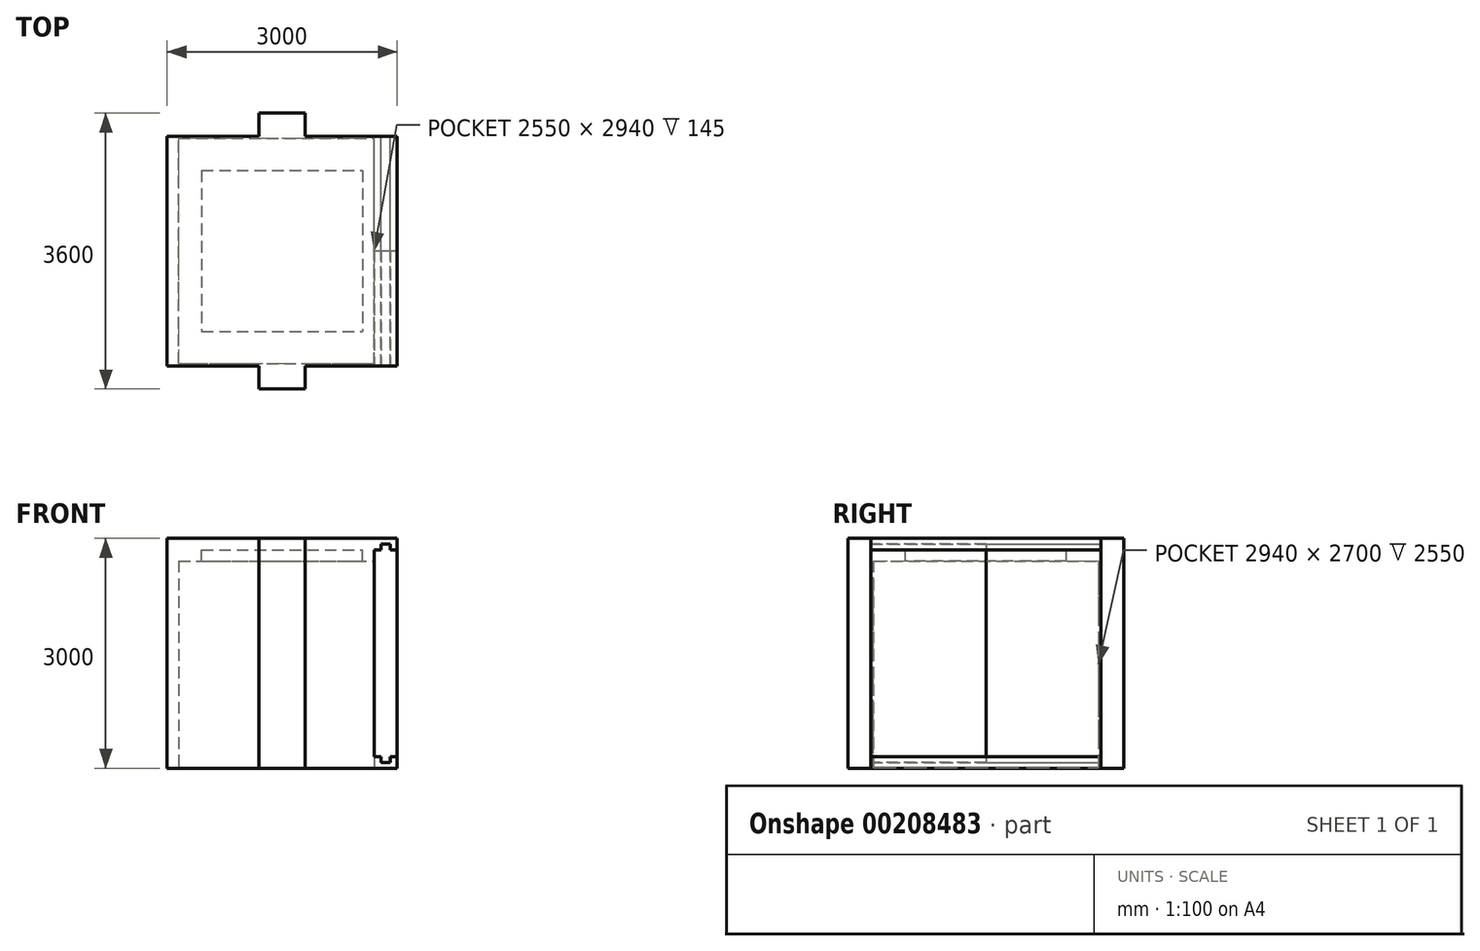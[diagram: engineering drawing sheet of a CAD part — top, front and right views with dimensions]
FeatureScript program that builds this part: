
annotation { "Feature Type Name" : "Feature", "Feature Type Description" : "" }
export const myFeature = defineFeature(function(context is Context, id is Id, definition is map)
    precondition{}
    {
        {
            var Q0;
            Q0=qCreatedBy(makeId("Top.planeOp"),FACE);
            var sketch = newSketch(context, id + "F0", { "sketchPlane" : qUnion([Q0])});
            skLineSegment(sketch, "E0.bottom", {"start": v(-1500, 1500) * mm, "end": v(1200, 1500) * mm});
            skLineSegment(sketch, "E0.top", {"start": v(-1500, -1500) * mm, "end": v(1200, -1500) * mm});
            skLineSegment(sketch, "E0.left", {"start": v(-1500, 1500) * mm, "end": v(-1500, -1500) * mm});
            skPoint(sketch, "E0.middle", {"position": v(0, 0) * mm});
            skLineSegment(sketch, "E1", {"start": v(-300, 1500) * mm, "end": v(-300, 1800) * mm});
            skLineSegment(sketch, "E2", {"start": v(-300, 1800) * mm, "end": v(300, 1800) * mm});
            skLineSegment(sketch, "E3", {"start": v(300, 1800) * mm, "end": v(300, 1500) * mm});
            skLineSegment(sketch, "E4.MirrorCS", {"start": v(-300, -1500) * mm, "end": v(-300, -1800) * mm});
            skLineSegment(sketch, "E5.MirrorCS", {"start": v(-300, -1800) * mm, "end": v(300, -1800) * mm});
            skLineSegment(sketch, "E6.MirrorCS", {"start": v(300, -1800) * mm, "end": v(300, -1500) * mm});
            skLineSegment(sketch, "E7", {"start": v(1200, 1500) * mm, "end": v(1200, -1500) * mm});
            skPoint(sketch, "E8.start.orphan", {"position": v(1200, 0) * mm});
            skSolve(sketch);
        }
        {
            var Q0;
            Q0=qSketchRegion(id+"F0",true);
            extrude(context, id + "F1", {"entities" : qUnion([Q0]), "depth" : 3000 * mm});
        }
        {
            var Q0;
            Q0=makeQuery(id+"F1.opExtrude","CAP_FACE",FACE,{"disambiguationData":[OSD([sQuery(id+"F0.wireOp",EDGE,"E0.bottom"),sQuery(id+"F0.wireOp",EDGE,"E0.top"),sQuery(id+"F0.wireOp",EDGE,"E0.left"),sQuery(id+"F0.wireOp",EDGE,"E0.right"),sQuery(id+"F0.wireOp",EDGE,"E1"),sQuery(id+"F0.wireOp",EDGE,"E2"),sQuery(id+"F0.wireOp",EDGE,"E3"),sQuery(id+"F0.wireOp",EDGE,"E4.MirrorCS"),sQuery(id+"F0.wireOp",EDGE,"E5.MirrorCS"),sQuery(id+"F0.wireOp",EDGE,"E6.MirrorCS")])],"isStart":false});
            var sketch = newSketch(context, id + "F2", { "sketchPlane" : qUnion([Q0])});
            skLineSegment(sketch, "E9.bottom", {"start": v(-1050, 1050) * mm, "end": v(1050, 1050) * mm});
            skLineSegment(sketch, "E9.top", {"start": v(-1050, -1050) * mm, "end": v(1050, -1050) * mm});
            skLineSegment(sketch, "E9.left", {"start": v(-1050, 1050) * mm, "end": v(-1050, -1050) * mm});
            skLineSegment(sketch, "E9.right", {"start": v(1050, 1050) * mm, "end": v(1050, -1050) * mm});
            skPoint(sketch, "E9.middle", {"position": v(0, 0) * mm});
            skSolve(sketch);
        }
        {
            var Q0;
            Q0=qSketchRegion(id+"F2",true);
            extrude(context, id + "F3", {"entities" : qUnion([Q0]), "operationType" : NewBodyOperationType.REMOVE, "oppositeDirection" : true, "depth" : 3000 * mm});
        }
        {
            var Q0;
            Q0=qCreatedBy(makeId("Top.planeOp"),FACE);
            var sketch = newSketch(context, id + "F4", { "sketchPlane" : qUnion([Q0])});
            skLineSegment(sketch, "E10.bottom", {"start": v(-1050, 1050) * mm, "end": v(1050, 1050) * mm});
            skLineSegment(sketch, "E10.top", {"start": v(-1050, -1050) * mm, "end": v(1050, -1050) * mm});
            skLineSegment(sketch, "E10.left", {"start": v(-1050, 1050) * mm, "end": v(-1050, -1050) * mm});
            skLineSegment(sketch, "E10.right", {"start": v(1050, 1050) * mm, "end": v(1050, -1050) * mm});
            skPoint(sketch, "E10.middle", {"position": v(0, 0) * mm});
            skSolve(sketch);
        }
        {
            var Q0;
            Q0=qSketchRegion(id+"F4",true);
            extrude(context, id + "F5", {"entities" : qUnion([Q0]), "operationType" : NewBodyOperationType.ADD, "depth" : 150 * mm});
        }
        {
            var Q0;
            Q0=makeQuery(id+"F1.opExtrude","CAP_FACE",FACE,{"disambiguationData":[OSD([sQuery(id+"F0.wireOp",EDGE,"E0.bottom"),sQuery(id+"F0.wireOp",EDGE,"E0.top"),sQuery(id+"F0.wireOp",EDGE,"E0.left"),sQuery(id+"F0.wireOp",EDGE,"E0.right"),sQuery(id+"F0.wireOp",EDGE,"E1"),sQuery(id+"F0.wireOp",EDGE,"E2"),sQuery(id+"F0.wireOp",EDGE,"E3"),sQuery(id+"F0.wireOp",EDGE,"E4.MirrorCS"),sQuery(id+"F0.wireOp",EDGE,"E5.MirrorCS"),sQuery(id+"F0.wireOp",EDGE,"E6.MirrorCS")])],"isStart":false});
            var sketch = newSketch(context, id + "F6", { "sketchPlane" : qUnion([Q0])});
            skLineSegment(sketch, "E11.bottom", {"start": v(-1050, 1050) * mm, "end": v(1050, 1050) * mm});
            skLineSegment(sketch, "E11.top", {"start": v(-1050, -1050) * mm, "end": v(1050, -1050) * mm});
            skLineSegment(sketch, "E11.left", {"start": v(-1050, 1050) * mm, "end": v(-1050, -1050) * mm});
            skLineSegment(sketch, "E11.right", {"start": v(1050, 1050) * mm, "end": v(1050, -1050) * mm});
            skPoint(sketch, "E11.middle", {"position": v(0, 0) * mm});
            skSolve(sketch);
        }
        {
            var Q0;
            Q0=qSketchRegion(id+"F6",true);
            extrude(context, id + "F7", {"entities" : qUnion([Q0]), "operationType" : NewBodyOperationType.ADD, "oppositeDirection" : true, "depth" : 150 * mm});
        }
        {
            var Q0;
            {var subQ0=sQuery(id+"F0.wireOp",EDGE,"E0.bottom");Q0=makeQuery(id+"F1.opExtrude","SWEPT_FACE",FACE,{"disambiguationData":[OSD([subQ0]),TDD([makeQuery(id+"F0.imprint","IMPRINT",EDGE,{"disambiguationData":[TD([[makeQuery(id+"F0.imprint","INTERSECT",VERTEX,{"derivedFrom":[subQ0,sQuery(id+"F0.wireOp",EDGE,"E7")]}),1.0]])],"derivedFrom":subQ0})])]});}
            var sketch = newSketch(context, id + "F8", { "sketchPlane" : qUnion([Q0])});
            skLineSegment(sketch, "E12", {"start": v(-1200, 3000) * mm, "end": v(-1500, 3000) * mm});
            skLineSegment(sketch, "E13", {"start": v(-1500, 3000) * mm, "end": v(-1500, 2850) * mm});
            skLineSegment(sketch, "E14", {"start": v(-1500, 2850) * mm, "end": v(-1410, 2850) * mm});
            skLineSegment(sketch, "E15", {"start": v(-1410, 2850) * mm, "end": v(-1410, 2925) * mm});
            skLineSegment(sketch, "E16", {"start": v(-1410, 2925) * mm, "end": v(-1290, 2925) * mm});
            skLineSegment(sketch, "E17", {"start": v(-1290, 2925) * mm, "end": v(-1290, 2850) * mm});
            skLineSegment(sketch, "E18", {"start": v(-1290, 2850) * mm, "end": v(-1200, 2850) * mm});
            skLineSegment(sketch, "E19", {"start": v(-1200, 3000) * mm, "end": v(-1200, 2850) * mm});
            skSolve(sketch);
        }
        {
            var Q0;
            Q0=qSketchRegion(id+"F8",true);
            extrude(context, id + "F9", {"entities" : qUnion([Q0]), "operationType" : NewBodyOperationType.ADD, "oppositeDirection" : true, "depth" : 3000 * mm});
        }
        {
            var Q0;
            Q0=makeQuery(id+"F1.opExtrude","SWEPT_FACE",FACE,{"disambiguationData":[OSD([sQuery(id+"F0.wireOp",EDGE,"E7")])]});
            var sketch = newSketch(context, id + "F10", { "sketchPlane" : qUnion([Q0])});
            skLineSegment(sketch, "E20.bottom", {"start": v(-1470, 2705) * mm, "end": v(1470, 2705) * mm});
            skLineSegment(sketch, "E20.top", {"start": v(-1470, 5) * mm, "end": v(1470, 5) * mm});
            skLineSegment(sketch, "E20.left", {"start": v(-1470, 2705) * mm, "end": v(-1470, 5) * mm});
            skLineSegment(sketch, "E20.right", {"start": v(1470, 2705) * mm, "end": v(1470, 5) * mm});
            skPoint(sketch, "E20.middle", {"position": v(0, 1355) * mm});
            skSolve(sketch);
        }
        {
            var Q0;
            Q0=qSketchRegion(id+"F10",true);
            extrude(context, id + "F11", {"entities" : qUnion([Q0]), "operationType" : NewBodyOperationType.REMOVE, "oppositeDirection" : true, "depth" : 2550 * mm});
        }
        {
            var Q0;
            {var subQ0=sQuery(id+"F0.wireOp",EDGE,"E0.bottom");Q0=makeQuery(id+"F9.boolean.opBoolean","MERGE",FACE,{"derivedFrom":[makeQuery(id+"F1.opExtrude","SWEPT_FACE",FACE,{"disambiguationData":[OSD([subQ0]),TDD([makeQuery(id+"F0.imprint","IMPRINT",EDGE,{"disambiguationData":[TD([[makeQuery(id+"F0.imprint","INTERSECT",VERTEX,{"derivedFrom":[subQ0,sQuery(id+"F0.wireOp",EDGE,"E7")]}),1.0]])],"derivedFrom":subQ0})])]}),makeQuery(id+"F9.opExtrude","CAP_FACE",FACE,{"disambiguationData":[OSD([sQuery(id+"F8.wireOp",EDGE,"E12"),sQuery(id+"F8.wireOp",EDGE,"E13"),sQuery(id+"F8.wireOp",EDGE,"E14"),sQuery(id+"F8.wireOp",EDGE,"E15"),sQuery(id+"F8.wireOp",EDGE,"E16"),sQuery(id+"F8.wireOp",EDGE,"E17"),sQuery(id+"F8.wireOp",EDGE,"E18"),sQuery(id+"F8.wireOp",EDGE,"E19")])],"isStart":true})]});}
            var sketch = newSketch(context, id + "F12", { "sketchPlane" : qUnion([Q0])});
            skLineSegment(sketch, "E21", {"start": v(-1200, 0) * mm, "end": v(-1500, 0) * mm});
            skLineSegment(sketch, "E22", {"start": v(-1500, 0) * mm, "end": v(-1500, 150) * mm});
            skLineSegment(sketch, "E23", {"start": v(-1500, 150) * mm, "end": v(-1410, 150) * mm});
            skLineSegment(sketch, "E24", {"start": v(-1410, 150) * mm, "end": v(-1410, 75) * mm});
            skLineSegment(sketch, "E25", {"start": v(-1410, 75) * mm, "end": v(-1290, 75) * mm});
            skLineSegment(sketch, "E26", {"start": v(-1290, 75) * mm, "end": v(-1290, 150) * mm});
            skLineSegment(sketch, "E27", {"start": v(-1290, 150) * mm, "end": v(-1200, 150) * mm});
            skLineSegment(sketch, "E28", {"start": v(-1200, 150) * mm, "end": v(-1200, 0) * mm});
            skSolve(sketch);
        }
        {
            var Q0;
            Q0=qSketchRegion(id+"F12",true);
            extrude(context, id + "F13", {"entities" : qUnion([Q0]), "operationType" : NewBodyOperationType.ADD, "oppositeDirection" : true, "depth" : 3000 * mm});
        }
        {
            var Q0;
            {var subQ0=sQuery(id+"F0.wireOp",EDGE,"E0.bottom");Q0=makeQuery(id+"F13.boolean.opBoolean","MERGE",FACE,{"derivedFrom":[makeQuery(id+"F9.boolean.opBoolean","MERGE",FACE,{"derivedFrom":[makeQuery(id+"F1.opExtrude","SWEPT_FACE",FACE,{"disambiguationData":[OSD([subQ0]),TDD([makeQuery(id+"F0.imprint","IMPRINT",EDGE,{"disambiguationData":[TD([[makeQuery(id+"F0.imprint","INTERSECT",VERTEX,{"derivedFrom":[subQ0,sQuery(id+"F0.wireOp",EDGE,"E7")]}),1.0]])],"derivedFrom":subQ0})])]}),makeQuery(id+"F9.opExtrude","CAP_FACE",FACE,{"disambiguationData":[OSD([sQuery(id+"F8.wireOp",EDGE,"E12"),sQuery(id+"F8.wireOp",EDGE,"E13"),sQuery(id+"F8.wireOp",EDGE,"E14"),sQuery(id+"F8.wireOp",EDGE,"E15"),sQuery(id+"F8.wireOp",EDGE,"E16"),sQuery(id+"F8.wireOp",EDGE,"E17"),sQuery(id+"F8.wireOp",EDGE,"E18"),sQuery(id+"F8.wireOp",EDGE,"E19")])],"isStart":true})]}),makeQuery(id+"F13.opExtrude","CAP_FACE",FACE,{"disambiguationData":[OSD([sQuery(id+"F12.wireOp",EDGE,"hug7QCPa-GxZ1-TSAt-IC7Z-w67bIKYh1you"),sQuery(id+"F12.wireOp",EDGE,"zlwaCWf6-FMFH-thxJ-zFcJ-GuFhcXhvfoc0"),sQuery(id+"F12.wireOp",EDGE,"0EdmMTyD-5i8C-5uJw-xAQZ-3ZzquauYSfZ3"),sQuery(id+"F12.wireOp",EDGE,"G8kcmfBX-Ja0w-3OlD-Dxyx-30gYmuTs85ml"),sQuery(id+"F12.wireOp",EDGE,"5mWS4ZSk-yXnk-gHQj-xdkv-r3xuj4l9kbUt"),sQuery(id+"F12.wireOp",EDGE,"H64zZp5d-78BU-SMuF-AOEI-HPVCNYyMH6M1"),sQuery(id+"F12.wireOp",EDGE,"DWSHwkkV-hsRF-nHit-ZVEL-xkg39FNqW3zN"),sQuery(id+"F12.wireOp",EDGE,"0eAQGVw0-3wB6-UMqD-h2DD-D08MPByl0bGS")])],"isStart":true})]});}
            var sketch = newSketch(context, id + "F14", { "sketchPlane" : qUnion([Q0])});
            skLineSegment(sketch, "E29", {"start": v(-1500, 2850) * mm, "end": v(-1410, 2850) * mm});
            skLineSegment(sketch, "E30", {"start": v(-1410, 2850) * mm, "end": v(-1410, 2925) * mm});
            skLineSegment(sketch, "E31", {"start": v(-1410, 2925) * mm, "end": v(-1290, 2925) * mm});
            skLineSegment(sketch, "E32", {"start": v(-1290, 2925) * mm, "end": v(-1290, 2850) * mm});
            skLineSegment(sketch, "E33", {"start": v(-1290, 2850) * mm, "end": v(-1200, 2850) * mm});
            skLineSegment(sketch, "E34", {"start": v(-1200, 2850) * mm, "end": v(-1200, 150) * mm});
            skLineSegment(sketch, "E35", {"start": v(-1200, 150) * mm, "end": v(-1290, 150) * mm});
            skLineSegment(sketch, "E36", {"start": v(-1290, 150) * mm, "end": v(-1290, 75) * mm});
            skLineSegment(sketch, "E37", {"start": v(-1290, 75) * mm, "end": v(-1410, 75) * mm});
            skLineSegment(sketch, "E38", {"start": v(-1410, 75) * mm, "end": v(-1410, 150) * mm});
            skLineSegment(sketch, "E39", {"start": v(-1410, 150) * mm, "end": v(-1500, 150) * mm});
            skLineSegment(sketch, "E40", {"start": v(-1500, 150) * mm, "end": v(-1500, 2850) * mm});
            skSolve(sketch);
        }
        {
            var Q0;
            Q0=qSketchRegion(id+"F14",true);
            extrude(context, id + "F15", {"entities" : qUnion([Q0]), "oppositeDirection" : true, "depth" : 1500 * mm});
        }
        {
            var Q0;
            {var subQ0=sQuery(id+"F0.wireOp",EDGE,"E0.top");Q0=makeQuery(id+"F13.boolean.opBoolean","MERGE",FACE,{"derivedFrom":[makeQuery(id+"F9.boolean.opBoolean","MERGE",FACE,{"derivedFrom":[makeQuery(id+"F1.opExtrude","SWEPT_FACE",FACE,{"disambiguationData":[OSD([subQ0]),TDD([makeQuery(id+"F0.imprint","IMPRINT",EDGE,{"disambiguationData":[TD([[makeQuery(id+"F0.imprint","INTERSECT",VERTEX,{"derivedFrom":[subQ0,sQuery(id+"F0.wireOp",EDGE,"E7")]}),1.0]])],"derivedFrom":subQ0})])]}),makeQuery(id+"F9.opExtrude","CAP_FACE",FACE,{"disambiguationData":[OSD([sQuery(id+"F8.wireOp",EDGE,"E12"),sQuery(id+"F8.wireOp",EDGE,"E13"),sQuery(id+"F8.wireOp",EDGE,"E14"),sQuery(id+"F8.wireOp",EDGE,"E15"),sQuery(id+"F8.wireOp",EDGE,"E16"),sQuery(id+"F8.wireOp",EDGE,"E17"),sQuery(id+"F8.wireOp",EDGE,"E18"),sQuery(id+"F8.wireOp",EDGE,"E19")])],"isStart":false})]}),makeQuery(id+"F13.opExtrude","CAP_FACE",FACE,{"disambiguationData":[OSD([sQuery(id+"F12.wireOp",EDGE,"hug7QCPa-GxZ1-TSAt-IC7Z-w67bIKYh1you"),sQuery(id+"F12.wireOp",EDGE,"zlwaCWf6-FMFH-thxJ-zFcJ-GuFhcXhvfoc0"),sQuery(id+"F12.wireOp",EDGE,"0EdmMTyD-5i8C-5uJw-xAQZ-3ZzquauYSfZ3"),sQuery(id+"F12.wireOp",EDGE,"G8kcmfBX-Ja0w-3OlD-Dxyx-30gYmuTs85ml"),sQuery(id+"F12.wireOp",EDGE,"5mWS4ZSk-yXnk-gHQj-xdkv-r3xuj4l9kbUt"),sQuery(id+"F12.wireOp",EDGE,"H64zZp5d-78BU-SMuF-AOEI-HPVCNYyMH6M1"),sQuery(id+"F12.wireOp",EDGE,"DWSHwkkV-hsRF-nHit-ZVEL-xkg39FNqW3zN"),sQuery(id+"F12.wireOp",EDGE,"0eAQGVw0-3wB6-UMqD-h2DD-D08MPByl0bGS")])],"isStart":false})]});}
            var sketch = newSketch(context, id + "F16", { "sketchPlane" : qUnion([Q0])});
            skLineSegment(sketch, "E41", {"start": v(1200, 2850) * mm, "end": v(1290, 2850) * mm});
            skLineSegment(sketch, "E42", {"start": v(1290, 2850) * mm, "end": v(1290, 2925) * mm});
            skLineSegment(sketch, "E43", {"start": v(1290, 2925) * mm, "end": v(1410, 2925) * mm});
            skLineSegment(sketch, "E44", {"start": v(1410, 2925) * mm, "end": v(1410, 2850) * mm});
            skLineSegment(sketch, "E45", {"start": v(1410, 2850) * mm, "end": v(1500, 2850) * mm});
            skLineSegment(sketch, "E46", {"start": v(1500, 2850) * mm, "end": v(1500, 150) * mm});
            skLineSegment(sketch, "E47", {"start": v(1500, 150) * mm, "end": v(1410, 150) * mm});
            skLineSegment(sketch, "E48", {"start": v(1410, 150) * mm, "end": v(1410, 75) * mm});
            skLineSegment(sketch, "E49", {"start": v(1410, 75) * mm, "end": v(1290, 75) * mm});
            skLineSegment(sketch, "E50", {"start": v(1290, 75) * mm, "end": v(1290, 150) * mm});
            skLineSegment(sketch, "E51", {"start": v(1290, 150) * mm, "end": v(1200, 150) * mm});
            skLineSegment(sketch, "E52", {"start": v(1200, 150) * mm, "end": v(1200, 2850) * mm});
            skSolve(sketch);
        }
        {
            var Q0;
            Q0=qSketchRegion(id+"F16",true);
            extrude(context, id + "F17", {"entities" : qUnion([Q0]), "oppositeDirection" : true, "depth" : 1500 * mm});
        }
    });
